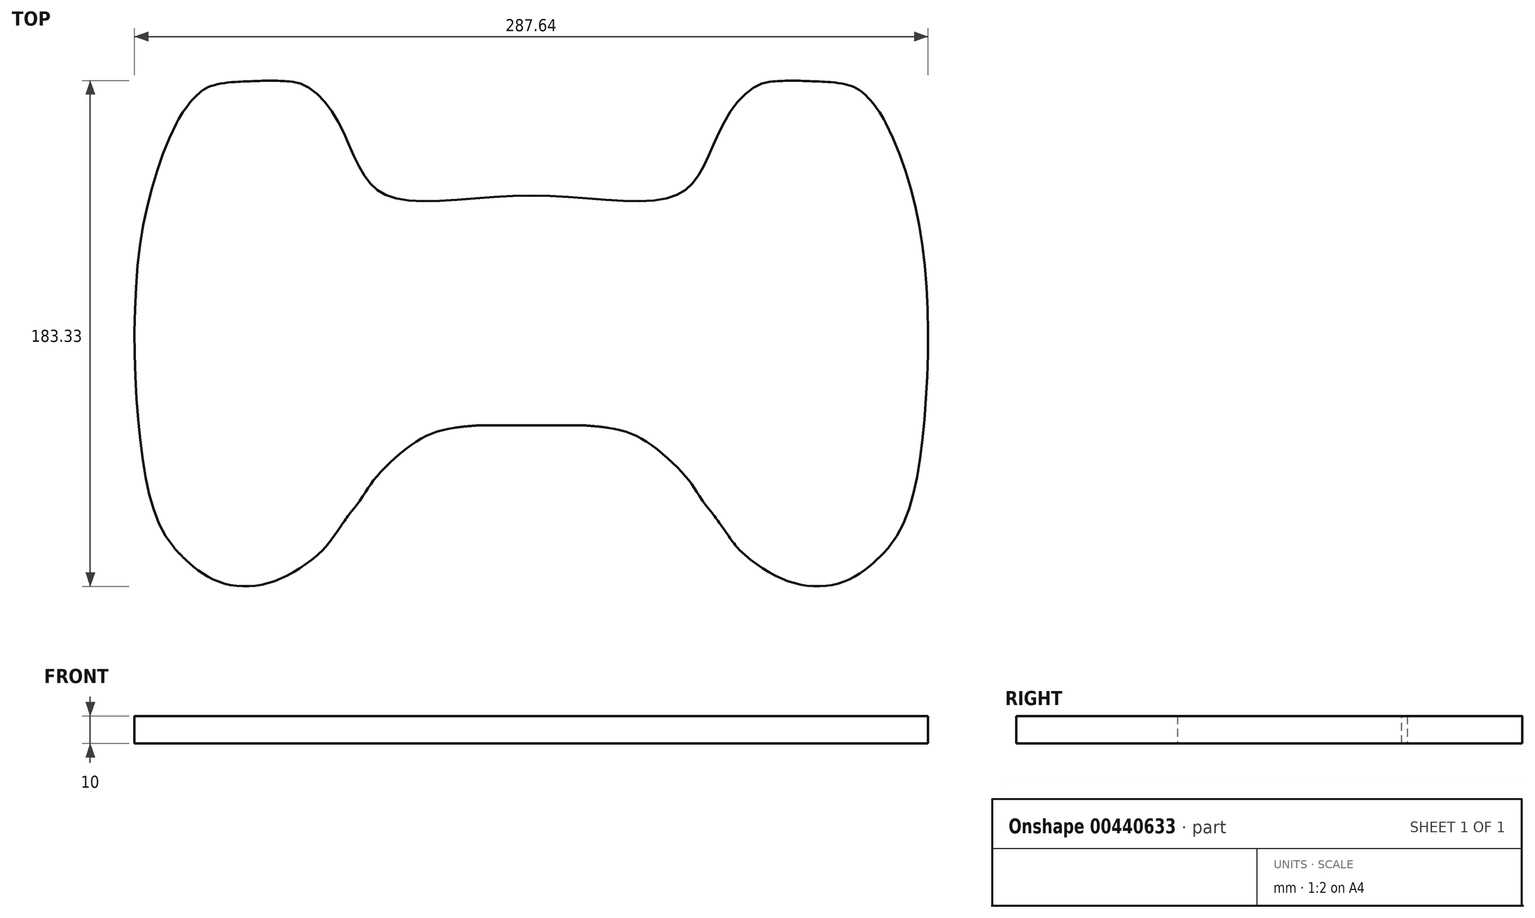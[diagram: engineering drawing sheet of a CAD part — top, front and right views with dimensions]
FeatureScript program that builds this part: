
annotation { "Feature Type Name" : "Feature", "Feature Type Description" : "" }
export const myFeature = defineFeature(function(context is Context, id is Id, definition is map)
    precondition{}
    {
        {
            var Q0;
            Q0=qCreatedBy(makeId("Top.planeOp"),FACE);
            var sketch = newSketch(context, id + "F0", { "sketchPlane" : qUnion([Q0])});
            skLineSegment(sketch, "E0", {"start": v(0, 0) * mm, "end": v(0, 39.85) * mm, "construction": true});
            skFitSpline(sketch, "E1", {"points": [v(0, 39.85) * mm, v(48.99, 38.8) * mm, v(61.86, 49.34) * mm, v(73.09, 71.67) * mm, v(86.58, 81.14) * mm], "startDerivative": vector(152.04, 0) * mm, "endDerivative": vector(66.68, 5.97) * mm});
            skFitSpline(sketch, "E2", {"points": [v(128.47, 66.29) * mm, v(142.32, 17.52) * mm, v(141.32, -52.28) * mm, v(129.53, -87.71) * mm], "startDerivative": vector(63.28, -128.05) * mm, "endDerivative": vector(-74.8, -89.53) * mm});
            skFitSpline(sketch, "E3", {"points": [v(75.4, -88.53) * mm, v(94.4, -100.39) * mm, v(111.3, -100.8) * mm, v(123.94, -93.37) * mm], "startDerivative": vector(46.48, -44.37) * mm, "endDerivative": vector(34.67, 31.98) * mm});
            skFitSpline(sketch, "E4", {"points": [v(65.56, -75.22) * mm, v(56.9, -63.1) * mm, v(42.81, -50.1) * mm, v(27.76, -44.34) * mm], "startDerivative": vector(-48.85, 58.54) * mm, "endDerivative": vector(-55.3, 7.57) * mm});
            skLineSegment(sketch, "E5", {"start": v(0, 0) * mm, "end": v(0, -43.42) * mm, "construction": true});
            skLineSegment(sketch, "E6", {"start": v(0, -43.42) * mm, "end": v(16.28, -43.42) * mm});
            skFitSpline(sketch, "E7", {"points": [v(65.56, -75.22) * mm, v(75.4, -88.53) * mm], "startDerivative": vector(5.73, -6.87) * mm, "endDerivative": vector(6.86, -6.55) * mm});
            skFitSpline(sketch, "E8", {"points": [v(123.94, -93.37) * mm, v(129.53, -87.71) * mm], "startDerivative": vector(6.38, 5.88) * mm, "endDerivative": vector(5.3, 6.34) * mm});
            skFitSpline(sketch, "E9", {"points": [v(128.47, 66.29) * mm, v(121.42, 76) * mm, v(115.85, 79.62) * mm, v(106.27, 81.12) * mm], "startDerivative": vector(-14.53, 29.4) * mm, "endDerivative": vector(-25.95, 1) * mm});
            skFitSpline(sketch, "E10", {"points": [v(86.58, 81.14) * mm, v(106.27, 81.12) * mm], "startDerivative": vector(21.96, 1.97) * mm, "endDerivative": vector(22.03, -0.85) * mm});
            skLineSegment(sketch, "E11", {"start": v(0, 39.85) * mm, "end": v(0, 39.85) * mm});
            skFitSpline(sketch, "E12", {"points": [v(16.28, -43.42) * mm, v(27.76, -44.34) * mm], "startDerivative": vector(11.52, 0) * mm, "endDerivative": vector(11.41, -1.56) * mm});
            skFitSpline(sketch, "E13.MirrorCS", {"points": [v(-123.94, -93.37) * mm, v(-129.53, -87.71) * mm], "startDerivative": vector(-6.38, 5.88) * mm, "endDerivative": vector(-5.3, 6.34) * mm});
            skFitSpline(sketch, "E14.MirrorCS", {"points": [v(-16.28, -43.42) * mm, v(-27.76, -44.34) * mm], "startDerivative": vector(-11.52, 0) * mm, "endDerivative": vector(-11.41, -1.56) * mm});
            skFitSpline(sketch, "E15.MirrorCS", {"points": [v(-75.4, -88.53) * mm, v(-94.4, -100.39) * mm, v(-111.3, -100.8) * mm, v(-123.94, -93.37) * mm], "startDerivative": vector(-46.48, -44.37) * mm, "endDerivative": vector(-34.67, 31.98) * mm});
            skLineSegment(sketch, "E16.MirrorCS", {"start": v(0, -43.42) * mm, "end": v(-16.28, -43.42) * mm});
            skFitSpline(sketch, "E17.MirrorCS", {"points": [v(-86.58, 81.14) * mm, v(-106.27, 81.12) * mm], "startDerivative": vector(-21.96, 1.97) * mm, "endDerivative": vector(-22.03, -0.85) * mm});
            skFitSpline(sketch, "E18.MirrorCS", {"points": [v(-128.47, 66.29) * mm, v(-121.42, 76) * mm, v(-115.85, 79.62) * mm, v(-106.27, 81.12) * mm], "startDerivative": vector(14.53, 29.4) * mm, "endDerivative": vector(25.95, 1) * mm});
            skFitSpline(sketch, "E19.MirrorCS", {"points": [v(-65.56, -75.22) * mm, v(-75.4, -88.53) * mm], "startDerivative": vector(-5.73, -6.87) * mm, "endDerivative": vector(-6.86, -6.55) * mm});
            skFitSpline(sketch, "E20.MirrorCS", {"points": [v(-128.47, 66.29) * mm, v(-142.32, 17.52) * mm, v(-141.32, -52.28) * mm, v(-129.53, -87.71) * mm], "startDerivative": vector(-63.28, -128.05) * mm, "endDerivative": vector(74.8, -89.53) * mm});
            skFitSpline(sketch, "E21.MirrorCS", {"points": [v(0, 39.85) * mm, v(-48.99, 38.8) * mm, v(-61.86, 49.34) * mm, v(-73.09, 71.67) * mm, v(-86.58, 81.14) * mm], "startDerivative": vector(-152.04, 0) * mm, "endDerivative": vector(-66.68, 5.97) * mm});
            skFitSpline(sketch, "E22.MirrorCS", {"points": [v(-65.56, -75.22) * mm, v(-56.9, -63.1) * mm, v(-42.81, -50.1) * mm, v(-27.76, -44.34) * mm], "startDerivative": vector(48.85, 58.54) * mm, "endDerivative": vector(55.3, 7.57) * mm});
            skSolve(sketch);
        }
        {
            var Q0;
            Q0=makeQuery(id+"F0.imprint","IMPRINT",FACE,{"disambiguationData":[TD([[makeQuery(id+"F0.imprint","IMPRINT",EDGE,{"derivedFrom":sQuery(id+"F0.wireOp",EDGE,"E1")}),-1.0]])]});
            extrude(context, id + "F1", {"entities" : qUnion([Q0]), "depth" : 10 * mm});
        }
    });
